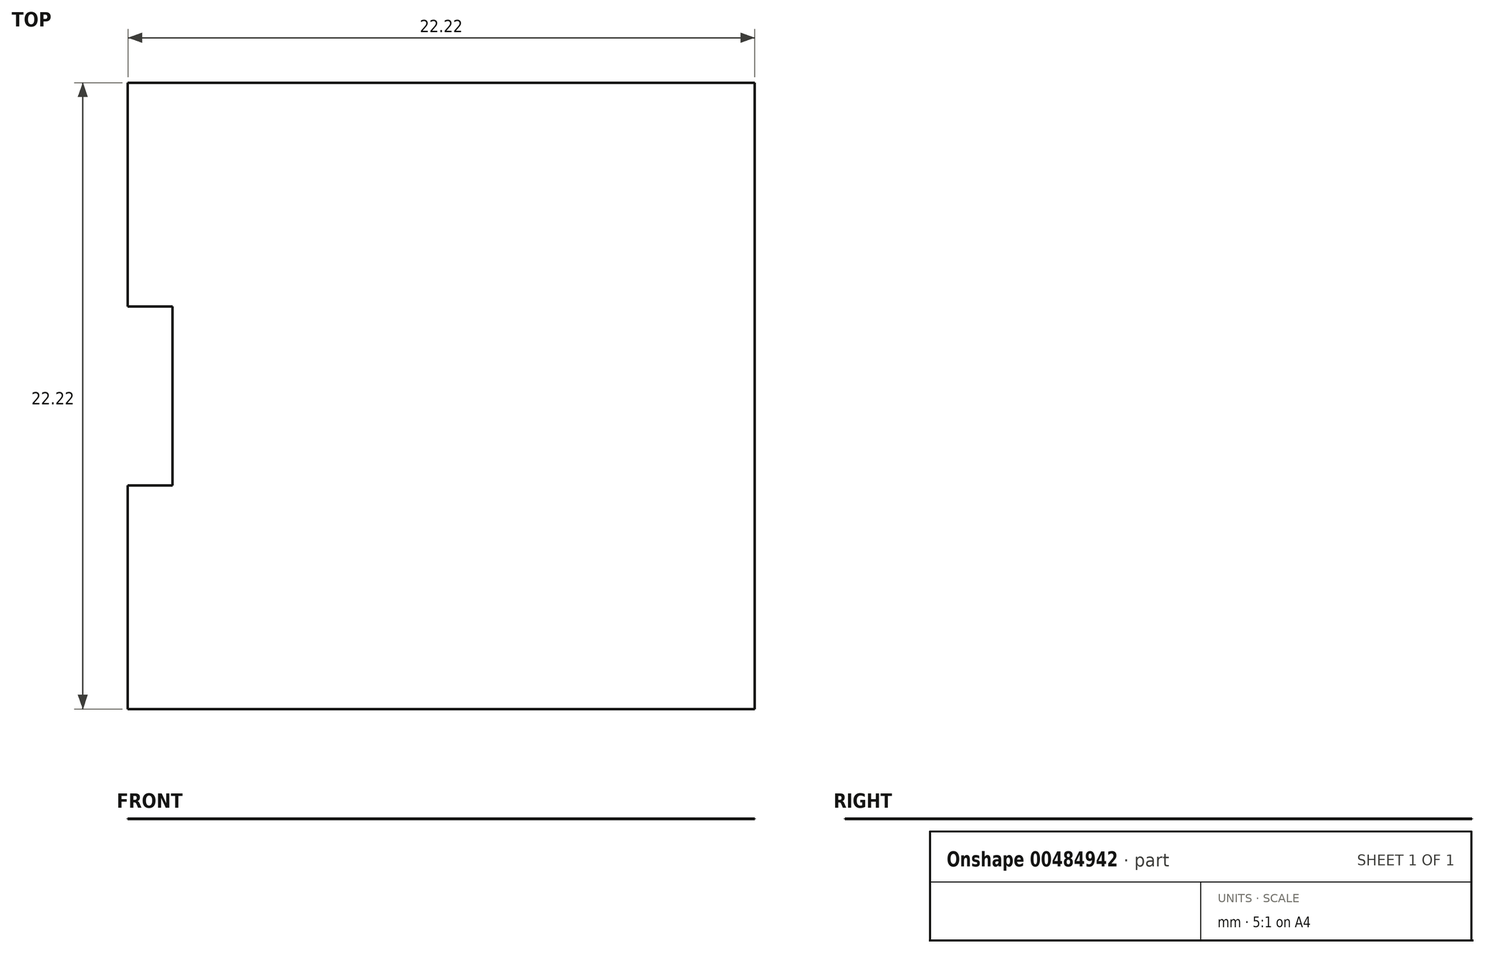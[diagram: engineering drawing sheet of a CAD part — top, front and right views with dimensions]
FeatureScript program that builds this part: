
annotation { "Feature Type Name" : "Feature", "Feature Type Description" : "" }
export const myFeature = defineFeature(function(context is Context, id is Id, definition is map)
    precondition{}
    {
        {
            var Q0;
            Q0=qCreatedBy(makeId("Top.planeOp"),FACE);
            var sketch = newSketch(context, id + "F0", { "sketchPlane" : qUnion([Q0])});
            skLineSegment(sketch, "E0.bottom", {"start": v(-11.11, -11.11) * mm, "end": v(11.11, -11.11) * mm});
            skLineSegment(sketch, "E0.top", {"start": v(-11.11, 11.11) * mm, "end": v(11.11, 11.11) * mm});
            skLineSegment(sketch, "E0.left", {"start": v(-11.11, -3.18) * mm, "end": v(-11.11, -11.11) * mm});
            skLineSegment(sketch, "E0.right", {"start": v(11.11, 11.11) * mm, "end": v(11.11, -11.11) * mm});
            skLineSegment(sketch, "E1.bottom", {"start": v(-11.11, 3.17) * mm, "end": v(-9.53, 3.17) * mm});
            skLineSegment(sketch, "E1.top", {"start": v(-11.11, -3.18) * mm, "end": v(-9.53, -3.18) * mm});
            skLineSegment(sketch, "E1.right", {"start": v(-9.53, 3.17) * mm, "end": v(-9.53, -3.17) * mm});
            skLineSegment(sketch, "E2.trimOffspring", {"start": v(-11.11, 11.11) * mm, "end": v(-11.11, 3.17) * mm});
            skSolve(sketch);
        }
        {
            var Q0;
            Q0 = qSketchRegion(id + "F0", true);
            extrude(context, id + "F1", {"entities" : qUnion([Q0]), "depth" : 1 / 406.4 * mm});
        }
    });
